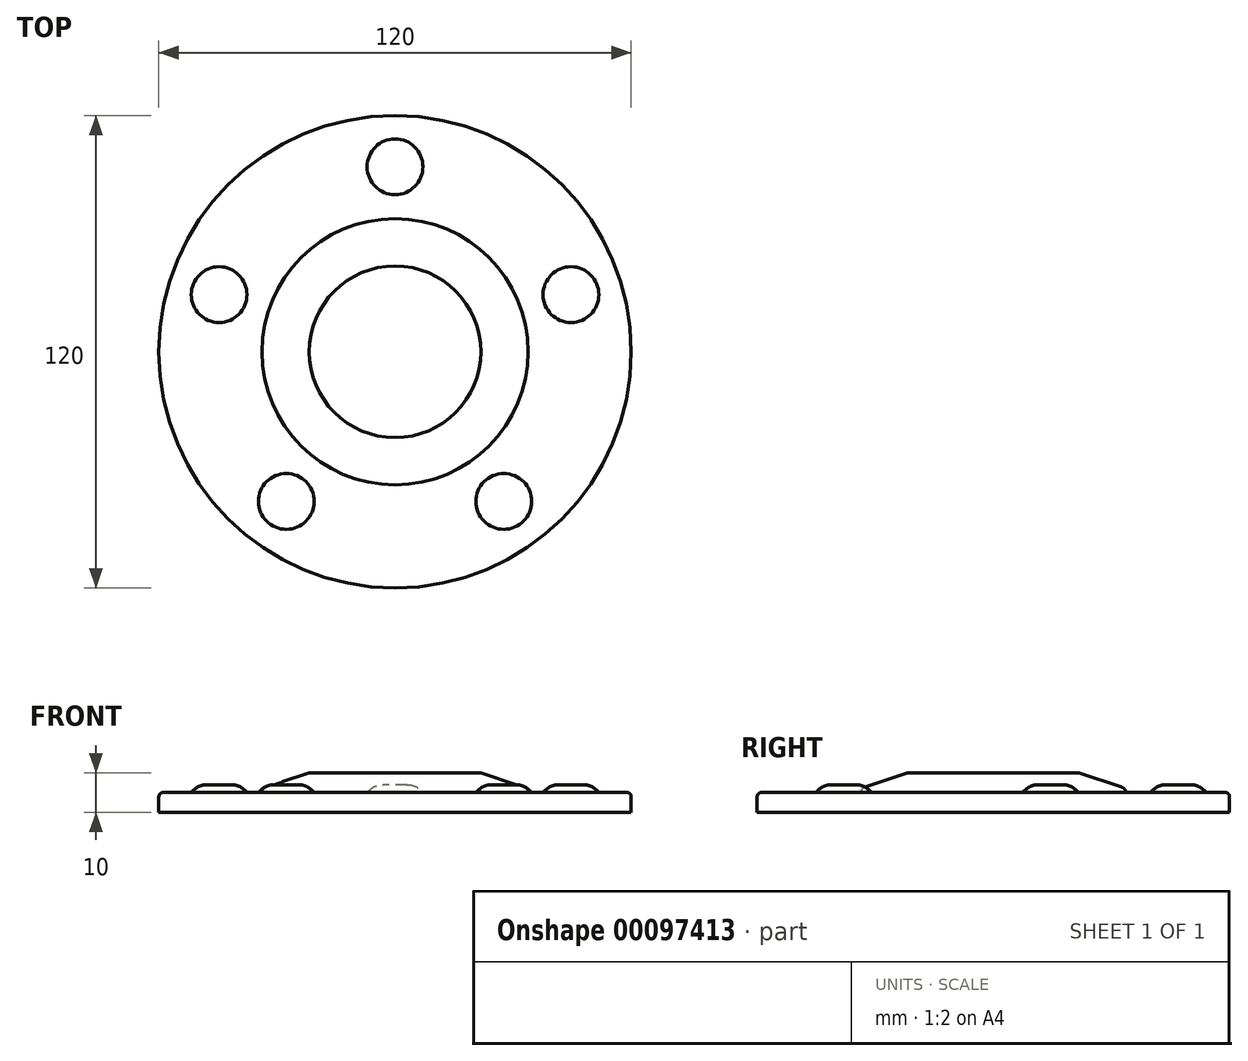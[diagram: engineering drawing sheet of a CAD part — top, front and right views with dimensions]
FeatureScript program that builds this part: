
annotation { "Feature Type Name" : "Feature", "Feature Type Description" : "" }
export const myFeature = defineFeature(function(context is Context, id is Id, definition is map)
    precondition{}
    {
        {
            var Q0;
            Q0=qCreatedBy(makeId("Top.planeOp"),FACE);
            var sketch = newSketch(context, id + "F0", { "sketchPlane" : qUnion([Q0])});
            skCircle(sketch, "E0", {"center": v(0, 0) * mm, "radius": 60 * mm});
            skSolve(sketch);
        }
        {
            var Q0;
            Q0=makeQuery(id+"F0.imprint","IMPRINT",FACE,{"disambiguationData":[TD([[makeQuery(id+"F0.imprint","IMPRINT",EDGE,{"derivedFrom":sQuery(id+"F0.wireOp",EDGE,"E0")}),1.0]])]});
            extrude(context, id + "F1", {"entities" : qUnion([Q0]), "depth" : 5 * mm});
        }
        {
            var Q0;
            Q0=makeQuery(id+"F1.opExtrude","CAP_EDGE",EDGE,{"disambiguationData":[OSD([sQuery(id+"F0.wireOp",EDGE,"E0")])],"isStart":false});
            fillet(context, id + "F2", {"entities" : qUnion([Q0]), "radius" : 1 * mm, "tangentPropagation" : true, "allowEdgeOverflow" : false});
        }
        {
            var Q0;
            Q0=makeQuery(id+"F1.opExtrude","CAP_FACE",FACE,{"disambiguationData":[OSD([sQuery(id+"F0.wireOp",EDGE,"E0")])],"isStart":false});
            var sketch = newSketch(context, id + "F3", { "sketchPlane" : qUnion([Q0])});
            skCircle(sketch, "E1", {"center": v(0, 47) * mm, "radius": 7.09 * mm});
            skCircle(sketch, "E2.1.0", {"center": v(-44.7, 14.52) * mm, "radius": 7.09 * mm});
            skCircle(sketch, "E2.2.0", {"center": v(-27.63, -38.02) * mm, "radius": 7.09 * mm});
            skPoint(sketch, "E2.center", {"position": v(0, 0) * mm});
            skCircle(sketch, "E3.1.3.0", {"center": v(27.63, -38.02) * mm, "radius": 7.09 * mm});
            skCircle(sketch, "E3.1.4.0", {"center": v(44.7, 14.52) * mm, "radius": 7.09 * mm});
            skSolve(sketch);
        }
        {
            var Q0;
            Q0=makeQuery(id+"F3.imprint","IMPRINT",FACE,{"disambiguationData":[TD([[makeQuery(id+"F3.imprint","IMPRINT",EDGE,{"derivedFrom":sQuery(id+"F3.wireOp",EDGE,"E1")}),1.0]])]});
            var Q1;
            Q1=makeQuery(id+"F3.imprint","IMPRINT",FACE,{"disambiguationData":[TD([[makeQuery(id+"F3.imprint","IMPRINT",EDGE,{"derivedFrom":sQuery(id+"F3.wireOp",EDGE,"E2.1.0")}),1.0]])]});
            var Q2;
            Q2=makeQuery(id+"F3.imprint","IMPRINT",FACE,{"disambiguationData":[TD([[makeQuery(id+"F3.imprint","IMPRINT",EDGE,{"derivedFrom":sQuery(id+"F3.wireOp",EDGE,"E2.2.0")}),1.0]])]});
            var Q3;
            Q3=makeQuery(id+"F3.imprint","IMPRINT",FACE,{"disambiguationData":[TD([[makeQuery(id+"F3.imprint","IMPRINT",EDGE,{"derivedFrom":sQuery(id+"F3.wireOp",EDGE,"E3.1.3.0")}),1.0]])]});
            var Q4;
            Q4=makeQuery(id+"F3.imprint","IMPRINT",FACE,{"disambiguationData":[TD([[makeQuery(id+"F3.imprint","IMPRINT",EDGE,{"derivedFrom":sQuery(id+"F3.wireOp",EDGE,"E3.1.4.0")}),1.0]])]});
            var Q5;
            Q5=makeQuery(id+"F3.imprint","IMPRINT",FACE,{"disambiguationData":[TD([[makeQuery(id+"F3.imprint","IMPRINT",EDGE,{"derivedFrom":sQuery(id+"F3.wireOp",EDGE,"E3.1.5.0")}),1.0]])]});
            var Q6;
            Q6=makeQuery(id+"F3.imprint","IMPRINT",FACE,{"disambiguationData":[TD([[makeQuery(id+"F3.imprint","IMPRINT",EDGE,{"derivedFrom":sQuery(id+"F3.wireOp",EDGE,"E3.1.6.0")}),1.0]])]});
            var Q7;
            Q7=makeQuery(id+"F3.imprint","IMPRINT",FACE,{"disambiguationData":[TD([[makeQuery(id+"F3.imprint","IMPRINT",EDGE,{"derivedFrom":sQuery(id+"F3.wireOp",EDGE,"E3.1.7.0")}),1.0]])]});
            extrude(context, id + "F4", {"entities" : qUnion([Q0, Q1, Q2, Q3, Q4, Q5, Q6, Q7]), "operationType" : NewBodyOperationType.ADD, "depth" : 2 * mm});
        }
        {
            var Q0;
            Q0=makeQuery(id+"F4.opExtrude","CAP_EDGE",EDGE,{"disambiguationData":[OSD([sQuery(id+"F3.wireOp",EDGE,"E1")])],"isStart":false});
            var Q1;
            Q1=makeQuery(id+"F4.opExtrude","CAP_EDGE",EDGE,{"disambiguationData":[OSD([sQuery(id+"F3.wireOp",EDGE,"E3.1.7.0")])],"isStart":false});
            var Q2;
            Q2=makeQuery(id+"F4.opExtrude","CAP_EDGE",EDGE,{"disambiguationData":[OSD([sQuery(id+"F3.wireOp",EDGE,"E3.1.6.0")])],"isStart":false});
            var Q3;
            Q3=makeQuery(id+"F4.opExtrude","CAP_EDGE",EDGE,{"disambiguationData":[OSD([sQuery(id+"F3.wireOp",EDGE,"E3.1.5.0")])],"isStart":false});
            var Q4;
            Q4=makeQuery(id+"F4.opExtrude","CAP_EDGE",EDGE,{"disambiguationData":[OSD([sQuery(id+"F3.wireOp",EDGE,"E3.1.4.0")])],"isStart":false});
            var Q5;
            Q5=makeQuery(id+"F4.opExtrude","CAP_EDGE",EDGE,{"disambiguationData":[OSD([sQuery(id+"F3.wireOp",EDGE,"E3.1.3.0")])],"isStart":false});
            var Q6;
            Q6=makeQuery(id+"F4.opExtrude","CAP_EDGE",EDGE,{"disambiguationData":[OSD([sQuery(id+"F3.wireOp",EDGE,"E2.2.0")])],"isStart":false});
            var Q7;
            Q7=makeQuery(id+"F4.opExtrude","CAP_EDGE",EDGE,{"disambiguationData":[OSD([sQuery(id+"F3.wireOp",EDGE,"E2.1.0")])],"isStart":false});
            fillet(context, id + "F5", {"entities" : qUnion([Q0, Q1, Q2, Q3, Q4, Q5, Q6, Q7]), "radius" : 5 * mm, "tangentPropagation" : true, "allowEdgeOverflow" : false});
        }
        {
            var Q0;
            Q0=makeQuery(id+"F1.opExtrude","CAP_FACE",FACE,{"disambiguationData":[OSD([sQuery(id+"F0.wireOp",EDGE,"E0")])],"isStart":false});
            var sketch = newSketch(context, id + "F6", { "sketchPlane" : qUnion([Q0])});
            skCircle(sketch, "E4", {"center": v(0, 0) * mm, "radius": 33.8 * mm});
            skSolve(sketch);
        }
        {
            var Q0;
            Q0=makeQuery(id+"F6.imprint","IMPRINT",FACE,{"disambiguationData":[TD([[makeQuery(id+"F6.imprint","IMPRINT",EDGE,{"derivedFrom":sQuery(id+"F6.wireOp",EDGE,"E4")}),1.0]])]});
            extrude(context, id + "F7", {"entities" : qUnion([Q0]), "operationType" : NewBodyOperationType.ADD, "depth" : 5 * mm});
        }
        {
            var Q0;
            Q0=makeQuery(id+"F7.opExtrude","CAP_EDGE",EDGE,{"disambiguationData":[OSD([sQuery(id+"F6.wireOp",EDGE,"E4")])],"isStart":false});
            chamfer(context, id + "F8", {"entities" : qUnion([Q0]), "chamferType" : ChamferType.TWO_OFFSETS, "width1" : 12 * mm, "oppositeDirection" : false, "width2" : 4 * mm, "tangentPropagation" : true});
        }
        {
            var Q0;
            {var subQ0=sQuery(id+"F6.wireOp",EDGE,"E4");Q0=makeQuery(id+"F8.opChamfer","BLEND_EDGE",EDGE,{"blendedFrom":[makeQuery(id+"F7.opExtrude","CAP_EDGE",EDGE,{"disambiguationData":[OSD([subQ0])],"isStart":false}),makeQuery(id+"F7.opExtrude","SWEPT_FACE",FACE,{"disambiguationData":[OSD([subQ0])]})],"blendedInto":[makeQuery(id+"F7.opExtrude","SWEPT_FACE",FACE,{"disambiguationData":[OSD([subQ0])]})]});}
            fillet(context, id + "F9", {"entities" : qUnion([Q0]), "radius" : 2 * mm, "tangentPropagation" : true, "allowEdgeOverflow" : false});
        }
    });
